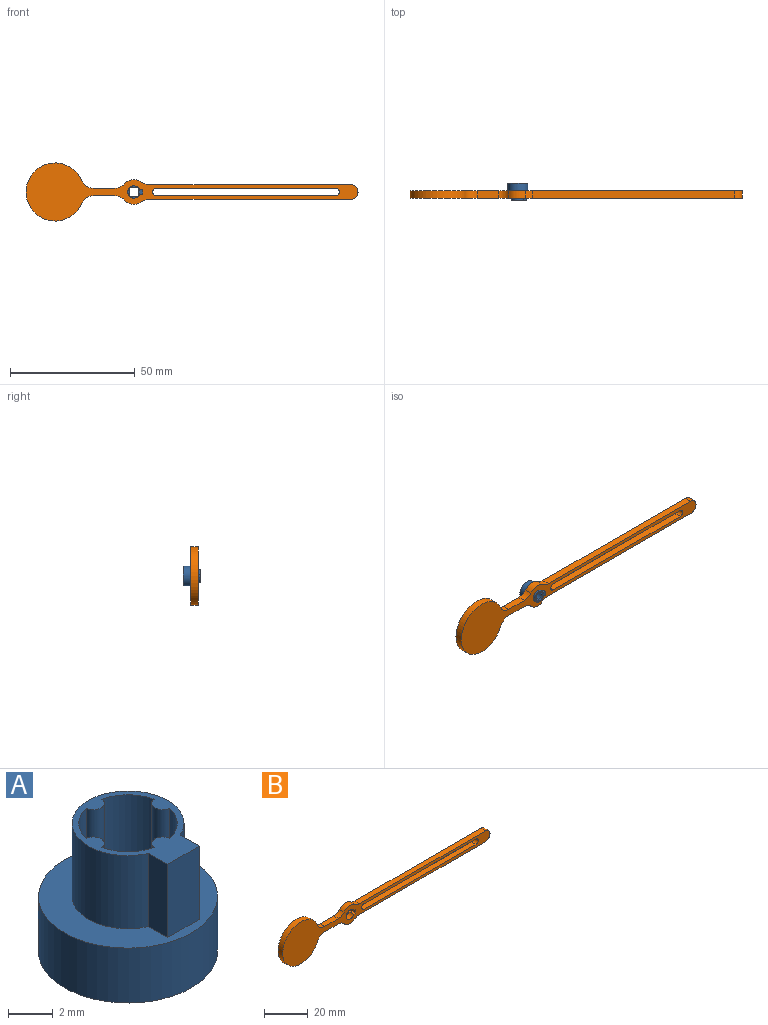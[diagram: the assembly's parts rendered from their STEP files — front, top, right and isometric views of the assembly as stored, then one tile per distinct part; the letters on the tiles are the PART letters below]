
ASSEMBLY  parts=2 mates=1
PART A: 18 faces, bbox 8x8x7 mm
  f0: cylinder r=2.2mm len=5mm, axis (0,0,-1), area 12.3mm2, adj f1,f7,f15,f17
  f1: cylinder r=0.5mm len=5mm, axis (0,0,-1), area 7.3mm2, adj f0,f2,f15,f17
  f2: cylinder r=2.2mm len=5mm, axis (0,0,-1), area 12.3mm2, adj f1,f3,f15,f17
  f3: cylinder r=0.5mm len=5mm, axis (0,0,-1), area 7.3mm2, adj f2,f4,f15,f17
  f4: cylinder r=2.2mm len=5mm, axis (0,0,-1), area 12.3mm2, adj f3,f5,f15,f17
  f5: cylinder r=0.5mm len=5mm, axis (0,0,-1), area 7.3mm2, adj f4,f6,f15,f17
  f6: cylinder r=2.2mm len=5mm, axis (0,0,-1), area 12.3mm2, adj f5,f7,f15,f17
  f7: cylinder r=0.5mm len=5mm, axis (0,0,-1), area 7.3mm2, adj f0,f6,f15,f17
  f8: cylinder r=4mm len=8mm, axis (0,0,-1), area 75.4mm2, adj f9,f10
  f9: plane 8x8mm, normal (0,0,1), area 28.5mm2, adj f8,f11,f12,f13,f14
  f10: plane 8x8mm, normal (0,0,-1), area 17.1mm2, adj f8,f16
  f11: cylinder r=2.5mm len=5mm, axis (0,0,-1), area 54.6mm2, adj f9,f12,f14,f15
  f12: plane 4x1.21mm, normal (-1,0,0), area 4.8mm2, adj f9,f11,f13,f15
  f13: plane 4x2mm, normal (0,-1,0), area 8mm2, adj f9,f12,f14,f15
  f14: plane 4x1.21mm, normal (1,0,0), area 4.8mm2, adj f9,f11,f13,f15
  f15: plane 6x5mm, normal (0,0,1), area 8.1mm2, adj f0,f1,f2,f3,f4,f5,f6,f7
  f16: cylinder r=3.25mm len=6.5mm, axis (0,0,1), area 40.8mm2, adj f10,f17
  f17: plane 6.5x6.5mm, normal (0,0,-1), area 19.5mm2, adj f0,f1,f2,f3,f4,f5,f6,f7
PART B: 24 faces, bbox 133.3x3x23.3 mm
  f0: plane 72x3mm, normal (0,0,-1), area 216mm2, adj f13,f14,f19,f20
  f1: plane 3x1.21mm, normal (0,0,1), area 3.6mm2, adj f2,f11,f13,f14
  f2: cylinder r=2.5mm len=5mm, axis (0,1,0), area 41mm2, adj f1,f3,f13,f14
  f3: plane 3x1.21mm, normal (0,0,-1), area 3.6mm2, adj f2,f11,f13,f14
  f4: cylinder r=11.67mm len=23.34mm, axis (0,1,0), area 191.9mm2, adj f13,f14,f22,f23
  f5: plane 8.72x3mm, normal (0,0,-1), area 26.2mm2, adj f13,f14,f17,f23
  f6: cylinder r=5mm len=6.8mm, axis (0,1,0), area 22.6mm2, adj f13,f14,f17,f18
  f7: plane 81x3mm, normal (0,0,-1), area 243mm2, adj f13,f14,f18,f21
  f8: plane 81x3mm, normal (0,0,1), area 243mm2, adj f13,f14,f15,f21
  f9: cylinder r=5mm len=6.8mm, axis (0,1,0), area 22.6mm2, adj f13,f14,f15,f16
  f10: plane 8.72x3mm, normal (0,0,1), area 26.2mm2, adj f13,f14,f16,f22
  f11: plane 3x2mm, normal (-1,0,0), area 6mm2, adj f1,f3,f13,f14
  f12: plane 72x3mm, normal (0,0,1), area 216mm2, adj f13,f14,f19,f20
  f13: plane 133.34x23.34mm, normal (0,-1,0), area 822.7mm2, adj f0,f1,f2,f3,f4,f5,f6,f7
  f14: plane 133.34x23.34mm, normal (0,1,0), area 822.7mm2, adj f0,f1,f2,f3,f4,f5,f6,f7
  f15: cylinder r=5mm len=3mm, axis (0,1,0), area 9.7mm2, adj f8,f9,f13,f14
  f16: cylinder r=5mm len=3.8mm, axis (0,1,0), area 12.9mm2, adj f9,f10,f13,f14
  f17: cylinder r=5mm len=3.8mm, axis (0,1,0), area 12.9mm2, adj f5,f6,f13,f14
  f18: cylinder r=5mm len=3mm, axis (0,1,0), area 9.7mm2, adj f6,f7,f13,f14
  f19: cylinder r=1.5mm len=3mm, axis (0,1,0), area 14.1mm2, adj f0,f12,f13,f14
  f20: cylinder r=1.5mm len=3mm, axis (0,1,0), area 14.1mm2, adj f0,f12,f13,f14
  f21: cylinder r=3mm len=6mm, axis (0,1,0), area 28.3mm2, adj f7,f8,f13,f14
  f22: cylinder r=5mm len=4.6mm, axis (0,1,0), area 17.6mm2, adj f4,f10,f13,f14
  f23: cylinder r=5mm len=4.6mm, axis (0,1,0), area 17.6mm2, adj f4,f5,f13,f14
PLACE A rot(axis=(0.58,-0.58,0.58),120deg) t=(-14.78,23.33,-0.16)mm
PLACE B t=(-14.78,19.03,-0.16)mm
MATE fastened A.f13 <-> B.f11  axis (1,0,0) through (-11.28,6.33,0.84)mm
